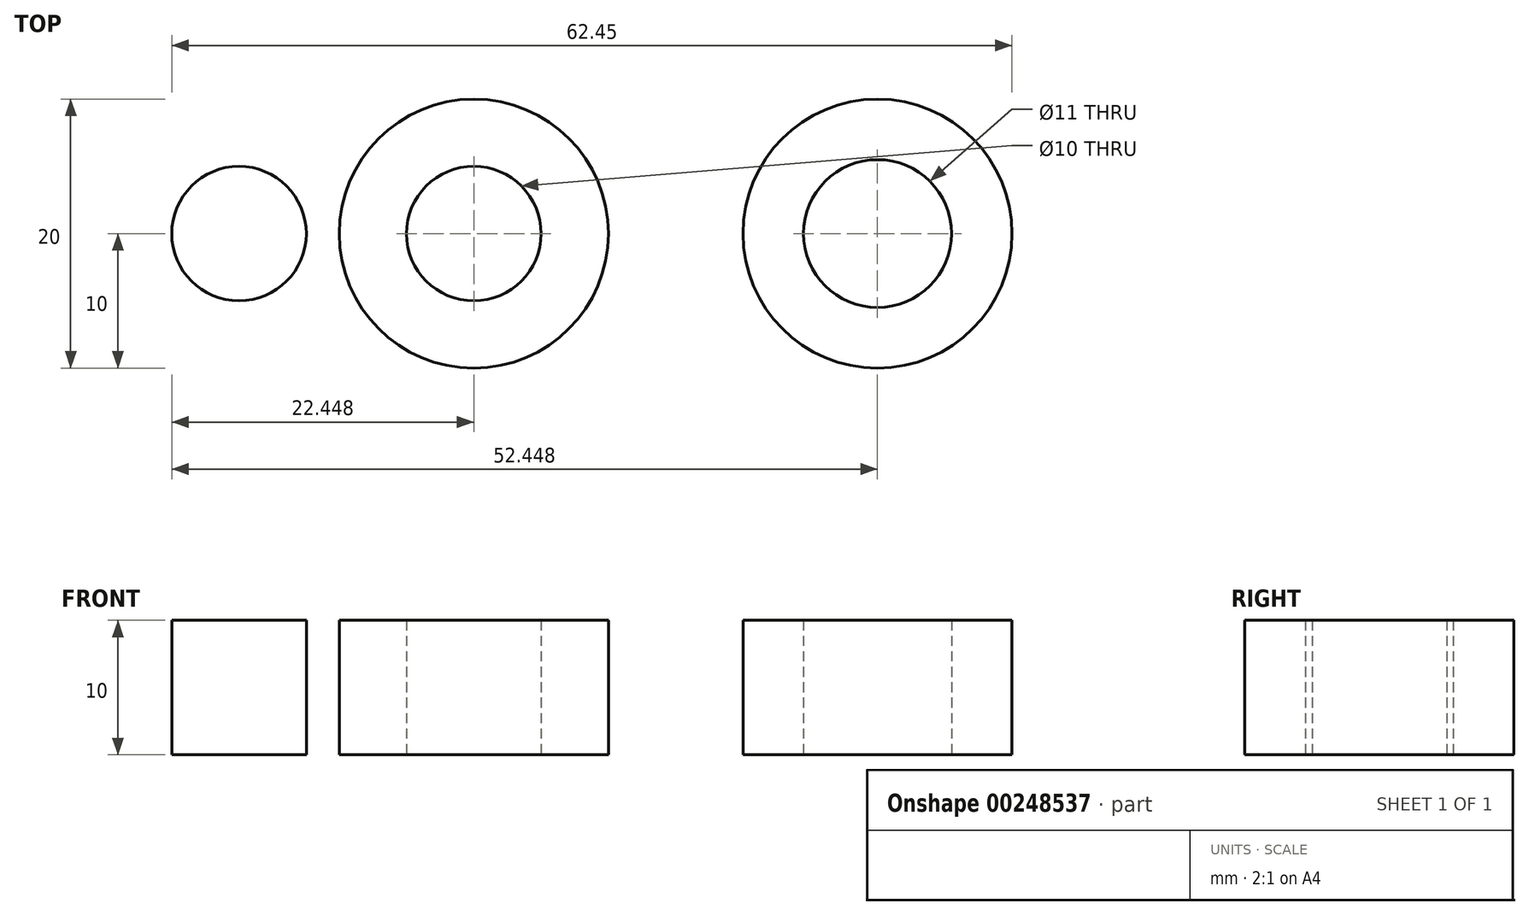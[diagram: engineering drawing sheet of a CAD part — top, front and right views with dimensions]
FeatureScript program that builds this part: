
annotation { "Feature Type Name" : "Feature", "Feature Type Description" : "" }
export const myFeature = defineFeature(function(context is Context, id is Id, definition is map)
    precondition{}
    {
        {
            assignVariable(context, id + "F0", {"name" : "h1", "anyValue" : 10});
        }
        {
            var Q0;
            Q0=qCreatedBy(makeId("Top.planeOp"),FACE);
            var sketch = newSketch(context, id + "F1", { "sketchPlane" : qUnion([Q0])});
            skCircle(sketch, "E0", {"center": v(0, 0) * mm, "radius": 5 * mm});
            skSolve(sketch);
        }
        {
            var Q0;
            Q0 = qSketchRegion(id + "F1", true);
            extrude(context, id + "F2", {"entities" : qUnion([Q0]), "depth" : (getVariable(context, 'h1')) * mm});
        }
        {
            var Q0;
            Q0=qCreatedBy(makeId("Top.planeOp"),FACE);
            var sketch = newSketch(context, id + "F3", { "sketchPlane" : qUnion([Q0])});
            skCircle(sketch, "E1", {"center": v(17.45, 0) * mm, "radius": 5 * mm});
            skCircle(sketch, "E2", {"center": v(17.45, 0) * mm, "radius": 10 * mm});
            skSolve(sketch);
        }
        {
            var Q0;
            Q0 = qSketchRegion(id + "F3", true);
            extrude(context, id + "F4", {"entities" : qUnion([Q0]), "depth" : (getVariable(context, 'h1')) * mm});
        }
        {
            var Q0;
            Q0=qCreatedBy(makeId("Top.planeOp"),FACE);
            var sketch = newSketch(context, id + "F5", { "sketchPlane" : qUnion([Q0])});
            skCircle(sketch, "E3", {"center": v(47.45, 0) * mm, "radius": 5.5 * mm});
            skCircle(sketch, "E4", {"center": v(47.45, 0) * mm, "radius": 10 * mm});
            skSolve(sketch);
        }
        {
            var Q0;
            Q0 = qSketchRegion(id + "F5", true);
            extrude(context, id + "F6", {"entities" : qUnion([Q0]), "depth" : (getVariable(context, 'h1')) * mm});
        }
    });
